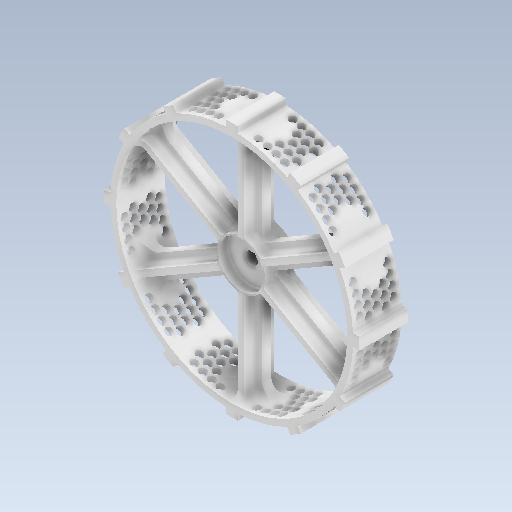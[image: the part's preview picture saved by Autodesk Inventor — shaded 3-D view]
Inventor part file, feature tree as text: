
AUTODESK INVENTOR PART (.ipt)
format: ipt  version: 2023 (Build 270158000, 158)  size: 1,769,472 bytes
history: native  units: in
note: dims shown in document units (in); Inventor stores cm internally (conversion verified against a paired STEP export)
features: extrude x7, fillet x7, sketch x7, pattern_circular x3, plane x2, mirror x1, projected_geometry x1
ambient origin geometry x8: Origin, YZ Plane, XZ Plane, XY Plane, X Axis, Y Axis, Z Axis, Center Point
bodies: Solid1 (feature_tree)
feature tree (28):
  extrude  "Extrusion1"  Depth=0.25in
  extrude  "Extrusion2"  Depth=2.0in
  extrude  "Extrusion4"  Depth=0.4375in
  extrude  "Extrusion5"  Depth=0.25in
  pattern_circular  "Circular Pattern1"  [2 undecoded]
  extrude  "Extrusion6"  Depth=2.3622in TaperAngle=360.0deg
  fillet  "Fillet9"  Radius=1.0in
  fillet  "Fillet10"  Radius=0.0625in
  fillet  "Fillet11"  Radius=0.5in
  fillet  "Fillet12"  Radius=0.25in
  fillet  "Fillet13"  Radius=0.125in
  fillet  "Fillet14"  Radius=0.125in
  fillet  "Fillet15"  Radius=0.25in
  extrude  "Extrusion7"  Depth=0.125in
  pattern_circular  "Circular Pattern2"  [2 undecoded]
  plane  "Work Plane1"
  extrude  "Extrusion8"  Depth=0.5in
  plane  "Work Plane2"
  mirror  "Mirror1"
  pattern_circular  "Circular Pattern3"  [2 undecoded]
  sketch  "Sketch1"  dims[d0=10.0in d1=0.25in]
  sketch  "Sketch2"  dims[d2=2.0in d3=0.0in d4=2.0in]
  sketch  "Sketch5"  dims[d6=0.875in d7=0.4375in]
  projected_geometry  "Projected Loop1"
  sketch  "Sketch6"  dims[d8=0.375in d9=0.0in d21=0.25in]
  sketch  "Sketch7"  dims[d22=0.125in]
  sketch  "Sketch8"  dims[d23=1.25in d24=0.0in]
  sketch  "Sketch11"  dims[d26=2.0in d27=1.25in d28=0.0in d31=2.3622in d32=360.0deg d35=1.0in d36=0.0in d43=0.0625in d44=0.5in d45=0.25in d46=0.125in d47=0.125in d48=0.25in d49=0.125in d50=0.125in d51=0.5in d52=0.25in d53=0.25in d54=0.0in d55=4.7244in d56=360.0deg d73=0.3125in d75=0.3125in d76=0.3125in d77=0.375in d78=0.375in d79=0.6005in d80=0.3125in d81=0.0in d82=0.35in d83=0.35in d84=0.35in d85=0.3125in d86=0.375in d87=0.3125in d88=0.35in d89=0.3125in d90=0.375in d91=0.5in d92=0.0in d93=0.4108in d94=0.35in d95=0.4156in d96=0.7906in d97=2.3622in d98=360.0deg d100=0.3125in d101=0.375in d102=0.3125in d103=0.375in d104=0.35in d105=0.35in d106=0.5in d29=0.0in d30=0.0in d37=0.5in d38=0.0344in d39=0.5in d40=0.0344in]
note: 6 required parameter values undecoded (feature->parameter linkage not recoverable at this tier; creation-order binding heuristic only, values carry confidence <= 0.55)
